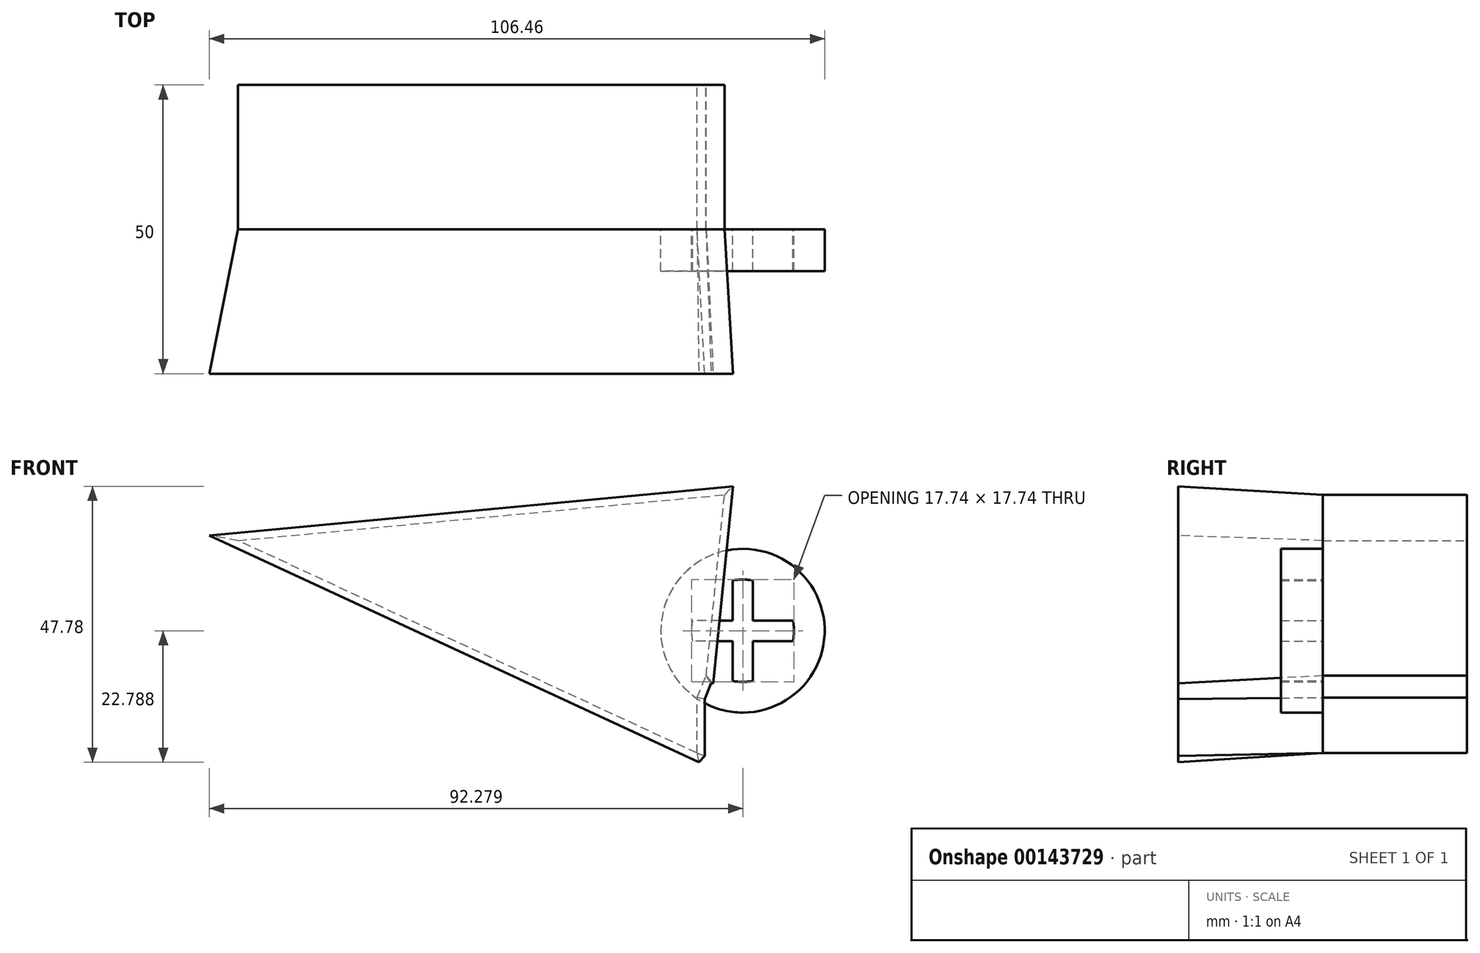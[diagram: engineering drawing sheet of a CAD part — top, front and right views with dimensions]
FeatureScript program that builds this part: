
annotation { "Feature Type Name" : "Feature", "Feature Type Description" : "" }
export const myFeature = defineFeature(function(context is Context, id is Id, definition is map)
    precondition{}
    {
        {
            var Q0;
            Q0=qCreatedBy(makeId("Front.planeOp"),FACE);
            var sketch = newSketch(context, id + "F0", { "sketchPlane" : qUnion([Q0])});
            skCircle(sketch, "E0", {"center": v(-19.47, 7.8) * mm, "radius": 14.18 * mm});
            skCircle(sketch, "E1", {"center": v(-19.47, 7.8) * mm, "radius": 8.87 * mm});
            skCircle(sketch, "E2", {"center": v(-19.47, 7.8) * mm, "radius": 1.78 * mm});
            skLineSegment(sketch, "E3", {"start": v(-21.25, 7.8) * mm, "end": v(-21.25, 16.5) * mm});
            skLineSegment(sketch, "E4", {"start": v(-21.25, 16.5) * mm, "end": v(-21.25, -0.88) * mm});
            skLineSegment(sketch, "E5", {"start": v(-21.25, -0.88) * mm, "end": v(-21.25, 16.5) * mm});
            skLineSegment(sketch, "E6", {"start": v(-17.7, 8) * mm, "end": v(-17.7, 16.5) * mm});
            skLineSegment(sketch, "E7", {"start": v(-17.7, 16.5) * mm, "end": v(-17.7, -0.88) * mm});
            skLineSegment(sketch, "E8", {"start": v(-17.7, -0.88) * mm, "end": v(-17.7, 16.5) * mm});
            skLineSegment(sketch, "E9", {"start": v(-19.47, 9.58) * mm, "end": v(-28.16, 9.58) * mm});
            skLineSegment(sketch, "E10", {"start": v(-28.16, 9.58) * mm, "end": v(-10.78, 9.58) * mm});
            skLineSegment(sketch, "E11", {"start": v(-10.78, 9.58) * mm, "end": v(-28.16, 9.58) * mm});
            skLineSegment(sketch, "E12", {"start": v(-19.47, 6.03) * mm, "end": v(-28.16, 6.03) * mm});
            skLineSegment(sketch, "E13", {"start": v(-28.16, 6.03) * mm, "end": v(-10.78, 6.03) * mm});
            skLineSegment(sketch, "E14", {"start": v(-10.78, 6.03) * mm, "end": v(-28.16, 6.03) * mm});
            skSolve(sketch);
        }
        {
            var Q0;
            Q0 = qSketchRegion(id + "F0", true);
            var Q1;
            {var subQ4=sQuery(id+"F0.wireOp",EDGE,"E5");var subQ5=sQuery(id+"F0.wireOp",EDGE,"E1");var subQ6=makeQuery(id+"F0.imprint","INTERSECT",VERTEX,{"disambiguationData":[OD(1.0)],"derivedFrom":[subQ5,subQ4]});Q1=makeQuery(id+"F0.imprint","IMPRINT",FACE,{"disambiguationData":[TD([[makeQuery(id+"F0.imprint","IMPRINT",EDGE,{"disambiguationData":[TD([[subQ6,1.0]])],"derivedFrom":subQ5}),1.0]])]});}
            var Q2;
            {var subQ3=sQuery(id+"F0.wireOp",EDGE,"E11");var subQ8=sQuery(id+"F0.wireOp",EDGE,"E1");var subQ9=makeQuery(id+"F0.imprint","INTERSECT",VERTEX,{"disambiguationData":[OD(0.0)],"derivedFrom":[subQ8,subQ3]});Q2=makeQuery(id+"F0.imprint","IMPRINT",FACE,{"disambiguationData":[TD([[makeQuery(id+"F0.imprint","IMPRINT",EDGE,{"disambiguationData":[TD([[subQ9,1.0]])],"derivedFrom":subQ8}),1.0]])]});}
            var Q3;
            {var subQ0=sQuery(id+"F0.wireOp",EDGE,"E11");var subQ1=sQuery(id+"F0.wireOp",EDGE,"E1");var subQ2=makeQuery(id+"F0.imprint","INTERSECT",VERTEX,{"disambiguationData":[OD(1.0)],"derivedFrom":[subQ1,subQ0]});Q3=makeQuery(id+"F0.imprint","IMPRINT",FACE,{"disambiguationData":[TD([[makeQuery(id+"F0.imprint","IMPRINT",EDGE,{"disambiguationData":[TD([[subQ2,-1.0]])],"derivedFrom":subQ1}),1.0]])]});}
            var Q4;
            {var subQ0=sQuery(id+"F0.wireOp",EDGE,"E2");var subQ1=makeQuery(id+"F0.imprint","IMPRINT",VERTEX,{"derivedFrom":subQ0});Q4=makeQuery(id+"F0.imprint","IMPRINT",FACE,{"disambiguationData":[TD([[makeQuery(id+"F0.imprint","IMPRINT",EDGE,{"disambiguationData":[TD([[subQ1,1.0]])],"derivedFrom":subQ0}),1.0]])]});}
            var Q5;
            {var subQ0=sQuery(id+"F0.wireOp",EDGE,"E14");var subQ9=makeQuery(id+"F0.imprint","IMPRINT",VERTEX,{"derivedFrom":subQ0});Q5=makeQuery(id+"F0.imprint","IMPRINT",FACE,{"disambiguationData":[TD([[makeQuery(id+"F0.imprint","IMPRINT",EDGE,{"disambiguationData":[TD([[subQ9,1.0]])],"derivedFrom":subQ0}),1.0]])]});}
            extrude(context, id + "F1", {"entities" : qUnion([Q0, Q1, Q2, Q3, Q4, Q5]), "depth" : 7.24 * mm});
        }
        {
            var Q0;
            Q0=qCreatedBy(makeId("Front.planeOp"),FACE);
            var sketch = newSketch(context, id + "F2", { "sketchPlane" : qUnion([Q0])});
            skLineSegment(sketch, "E15", {"start": v(0, 0) * mm, "end": v(-25.83, 0) * mm});
            skLineSegment(sketch, "E16", {"start": v(-25.83, -0.48) * mm, "end": v(-22.36, 34.03) * mm});
            skLineSegment(sketch, "E17", {"start": v(-22.36, 34.03) * mm, "end": v(5.78, 34.03) * mm});
            skLineSegment(sketch, "E18", {"start": v(5.78, 34.03) * mm, "end": v(2.7, -8.96) * mm});
            skLineSegment(sketch, "E19", {"start": v(2.7, -9.54) * mm, "end": v(-16, -8) * mm});
            skLineSegment(sketch, "E20", {"start": v(-15.62, -8) * mm, "end": v(-17.54, -2.8) * mm});
            skLineSegment(sketch, "E21", {"start": v(-17.54, -2.8) * mm, "end": v(-27.57, -13.6) * mm});
            skLineSegment(sketch, "E22", {"start": v(-27.37, -13.4) * mm, "end": v(-27.37, -3.76) * mm});
            skLineSegment(sketch, "E23", {"start": v(-27.37, -3.76) * mm, "end": v(-20.63, -2.8) * mm});
            skLineSegment(sketch, "E24", {"start": v(-20.63, -2.22) * mm, "end": v(0, 0) * mm});
            skLineSegment(sketch, "E25", {"start": v(-27.37, -3.76) * mm, "end": v(-25.83, 0) * mm});
            skLineSegment(sketch, "E26", {"start": v(-106.8, 23.42) * mm, "end": v(5.78, 34.03) * mm});
            skLineSegment(sketch, "E27", {"start": v(-106.8, 23.42) * mm, "end": v(-27.37, -13.4) * mm});
            skSolve(sketch);
        }
        {
            var Q0;
            {var subQ0=sQuery(id+"F2.wireOp",EDGE,"E25");Q0=makeQuery(id+"F2.imprint","IMPRINT",FACE,{"disambiguationData":[TD([[makeQuery(id+"F2.imprint","IMPRINT",EDGE,{"derivedFrom":subQ0}),1.0]])]});}
            var Q1;
            {var subQ0=sQuery(id+"F2.wireOp",EDGE,"E25");Q1=makeQuery(id+"F2.imprint","IMPRINT",FACE,{"disambiguationData":[TD([[makeQuery(id+"F2.imprint","IMPRINT",EDGE,{"derivedFrom":subQ0}),1.0]])]});}
            extrude(context, id + "F3", {"entities" : qUnion([Q0, Q1]), "depth" : 25 * mm, "hasDraft" : true, "draftAngle" : 3 * degree, "hasSecondDirection" : true, "secondDirectionOppositeDirection" : true, "secondDirectionDepth" : 25 * mm});
        }
    });
